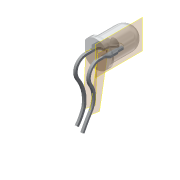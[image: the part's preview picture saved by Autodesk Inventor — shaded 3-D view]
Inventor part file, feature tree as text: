
AUTODESK INVENTOR PART (.ipt)
format: ipt  version: 2016 (Build 200138000, 138)  size: 374,784 bytes
history: native  units: mm
features: other x6, sketch x5, plane x3
ambient origin geometry x8: Origin, YZ Plane, XZ Plane, XY Plane, X Axis, Y Axis, Z Axis, Center Point
bodies: Solid1 (feature_tree), Solid2 (feature_tree)
feature tree (14):
  other  "5mm LED_MIR.ipt"
  other  "Solid1::5mm LED_MIR.ipt"
  other  "Solid2::5mm LED_MIR.ipt"
  other  "TaggingFeature1"
  sketch  "Sketch1"  dims[d0=10.0mm]
  sketch  "Sketch2"
  sketch  "Sketch4"
  sketch  "Sketch5"
  sketch  "Sketch6"
  plane  "Work Plane1"
  plane  "Work Plane2"
  plane  "Work Plane3"
  other  "Work Point1"
  other  "Work Point2"
